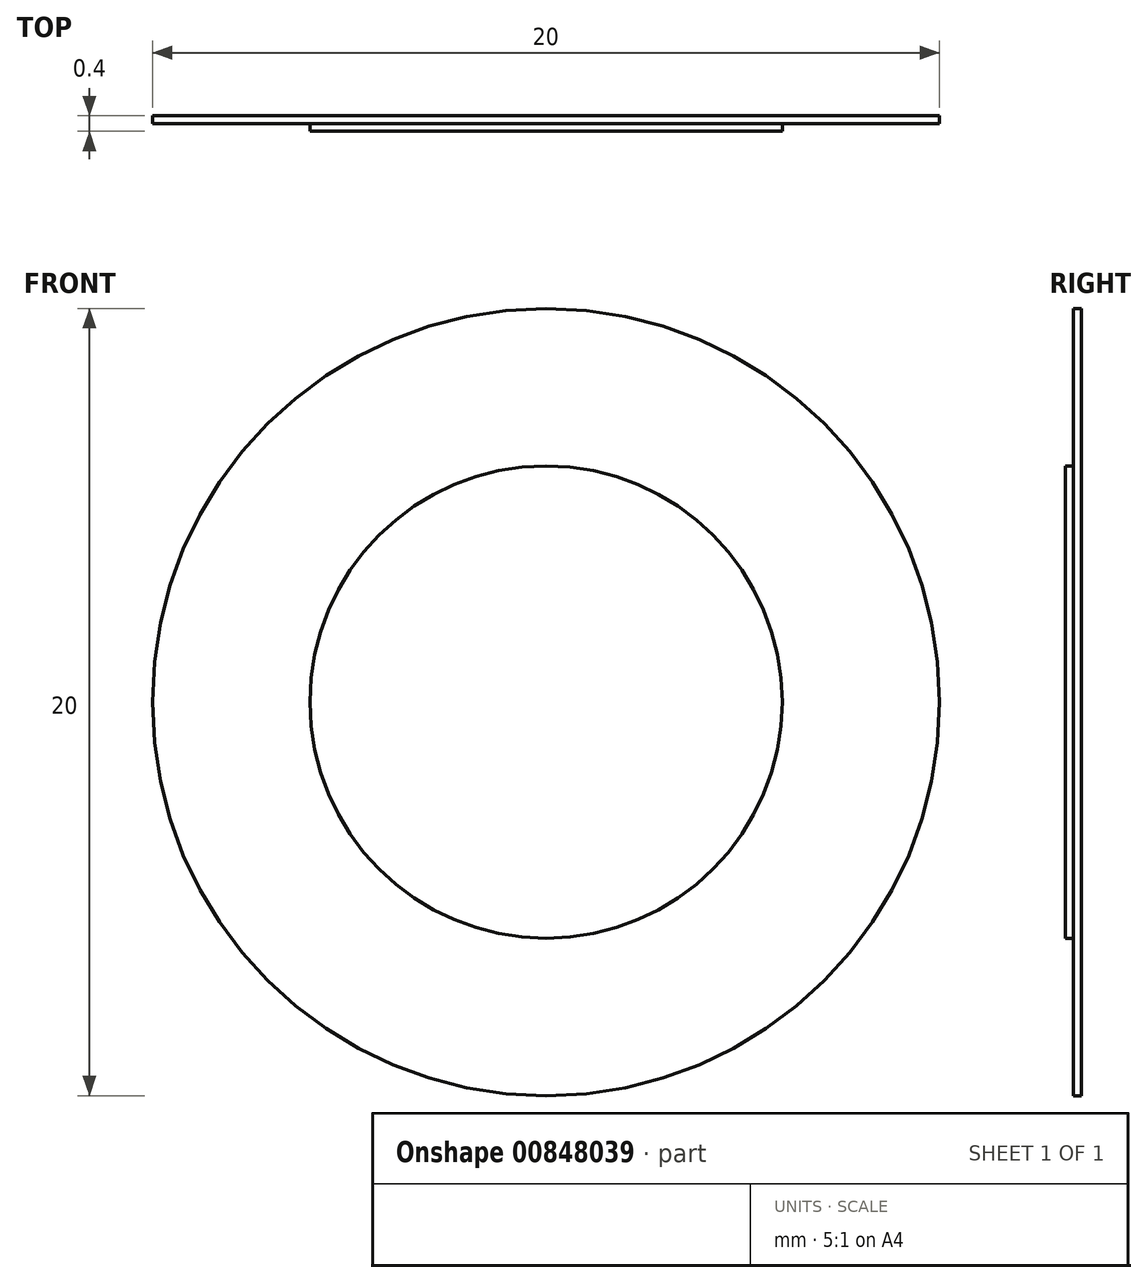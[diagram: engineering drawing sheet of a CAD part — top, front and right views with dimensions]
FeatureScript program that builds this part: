
annotation { "Feature Type Name" : "Feature", "Feature Type Description" : "" }
export const myFeature = defineFeature(function(context is Context, id is Id, definition is map)
    precondition{}
    {
        {
            var Q0;
            Q0=qCreatedBy(makeId("Front.planeOp"),FACE);
            var sketch = newSketch(context, id + "F0", { "sketchPlane" : qUnion([Q0])});
            skCircle(sketch, "E0", {"center": v(0, 0) * mm, "radius": 10 * mm});
            skCircle(sketch, "E1", {"center": v(0, 0) * mm, "radius": 6 * mm});
            skSolve(sketch);
        }
        {
            var Q0;
            Q0=makeQuery(id+"F0.imprint","IMPRINT",FACE,{"disambiguationData":[TD([[makeQuery(id+"F0.imprint","IMPRINT",EDGE,{"derivedFrom":sQuery(id+"F0.wireOp",EDGE,"E0")}),1.0]])]});
            extrude(context, id + "F1", {"entities" : qUnion([Q0]), "depth" : .2 * mm, "offsetDistance" : 25 * mm});
        }
        {
            var Q0;
            Q0=makeQuery(id+"F0.imprint","IMPRINT",FACE,{"disambiguationData":[TD([[makeQuery(id+"F0.imprint","IMPRINT",EDGE,{"derivedFrom":sQuery(id+"F0.wireOp",EDGE,"E1")}),1.0]])]});
            extrude(context, id + "F2", {"entities" : qUnion([Q0]), "operationType" : NewBodyOperationType.ADD, "depth" : .4 * mm, "offsetDistance" : 25 * mm});
        }
    });
